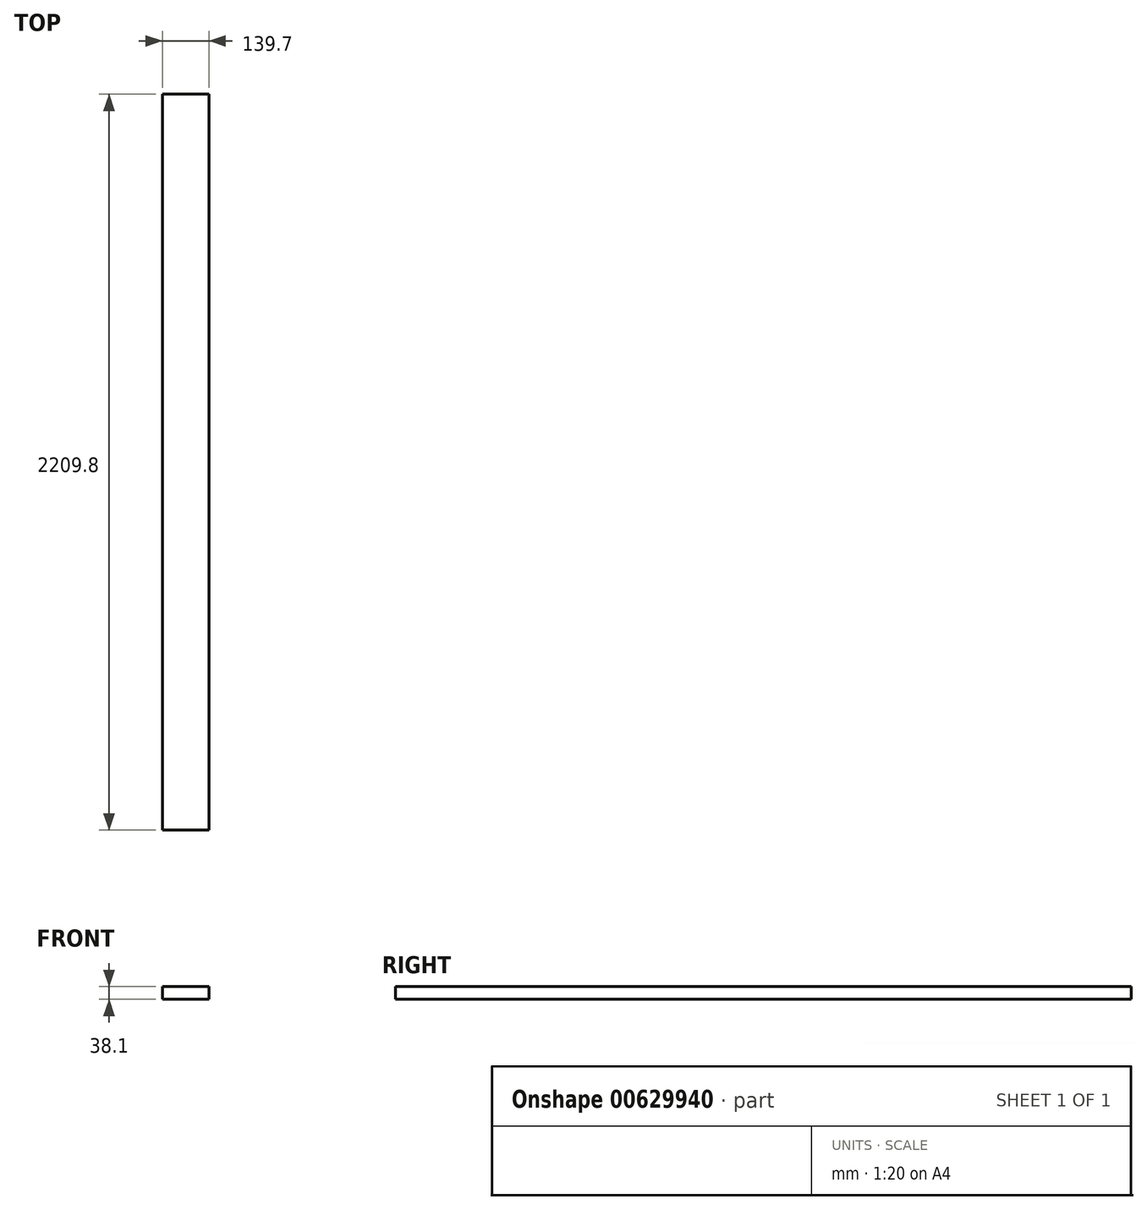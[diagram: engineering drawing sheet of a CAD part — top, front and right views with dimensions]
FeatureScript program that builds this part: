
annotation { "Feature Type Name" : "Feature", "Feature Type Description" : "" }
export const myFeature = defineFeature(function(context is Context, id is Id, definition is map)
    precondition{}
    {
        {
            var Q0;
            Q0=qCreatedBy(makeId("Front.planeOp"),FACE);
            var sketch = newSketch(context, id + "F0", { "sketchPlane" : qUnion([Q0])});
            skLineSegment(sketch, "E0.bottom", {"start": v(-74.4, 9.4) * mm, "end": v(65.3, 9.4) * mm});
            skLineSegment(sketch, "E0.top", {"start": v(-74.4, -28.7) * mm, "end": v(65.3, -28.7) * mm});
            skLineSegment(sketch, "E0.left", {"start": v(-74.4, 9.4) * mm, "end": v(-74.4, -28.7) * mm});
            skLineSegment(sketch, "E0.right", {"start": v(65.3, 9.4) * mm, "end": v(65.3, -28.7) * mm});
            skSolve(sketch);
        }
        {
            var Q0;
            Q0=qSketchRegion(id+"F0",true);
            extrude(context, id + "F1", {"entities" : qUnion([Q0]), "depth" : 2209.8 * mm, "offsetDistance" : 25.4 * mm});
        }
    });
